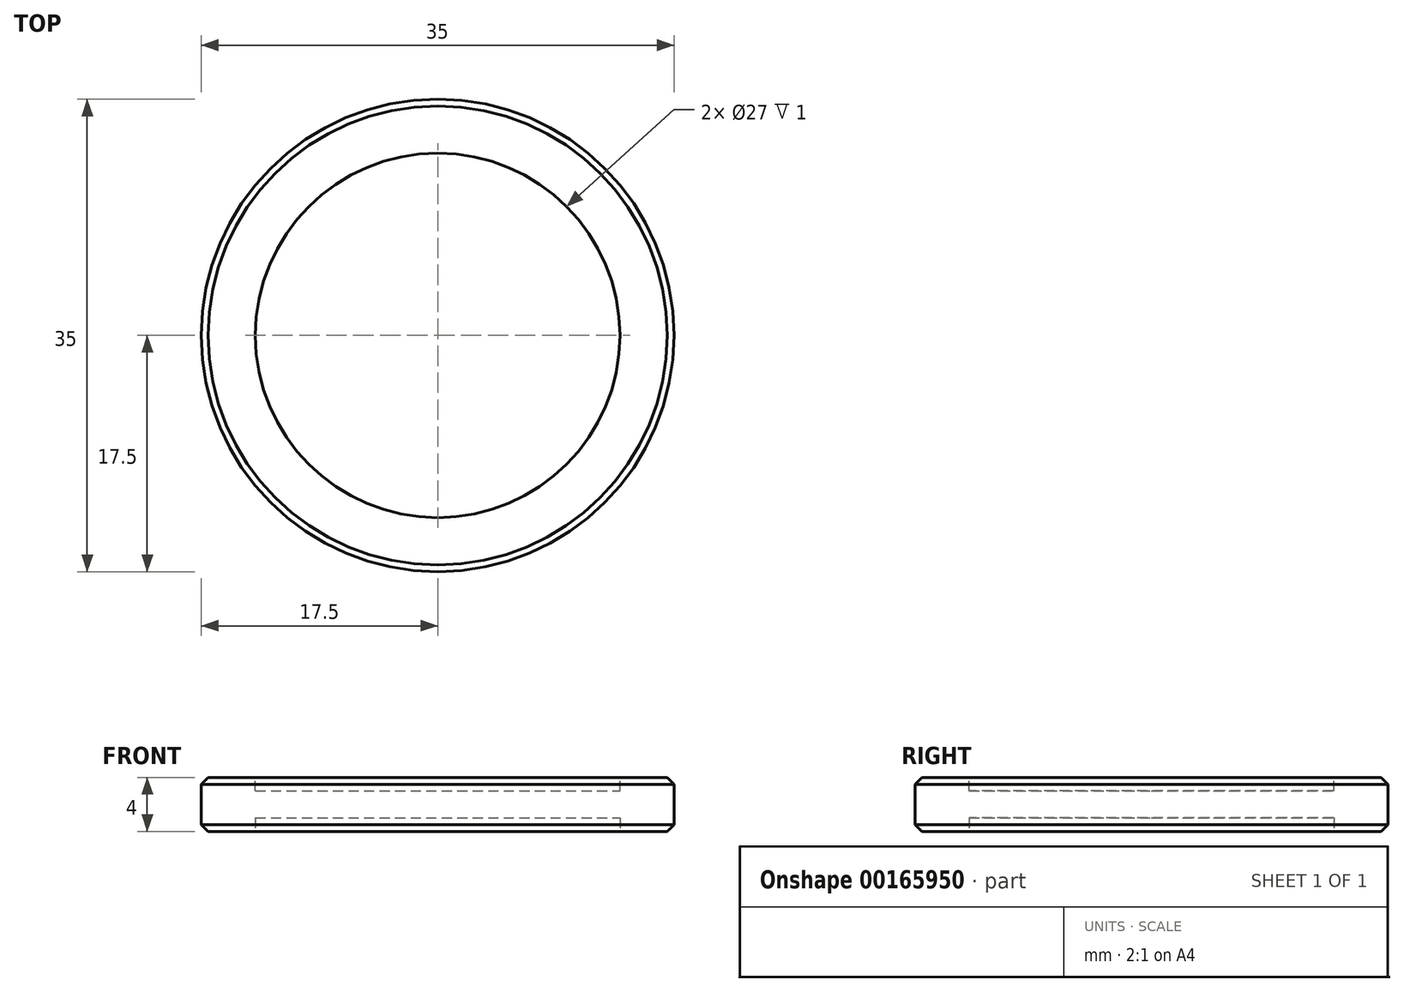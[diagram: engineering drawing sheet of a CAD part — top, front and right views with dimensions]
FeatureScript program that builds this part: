
annotation { "Feature Type Name" : "Feature", "Feature Type Description" : "" }
export const myFeature = defineFeature(function(context is Context, id is Id, definition is map)
    precondition{}
    {
        {
            var Q0;
            Q0=qCreatedBy(makeId("Top.planeOp"),FACE);
            var sketch = newSketch(context, id + "F0", { "sketchPlane" : qUnion([Q0])});
            skCircle(sketch, "E0", {"center": v(0, 0) * mm, "radius": 17.5 * mm});
            skSolve(sketch);
        }
        {
            var Q0;
            Q0 = qSketchRegion(id + "F0", true);
            extrude(context, id + "F1", {"entities" : qUnion([Q0]), "depth" : 2 * mm});
        }
        {
            var Q0;
            Q0=makeQuery(id+"F1.opExtrude","CAP_FACE",FACE,{"disambiguationData":[OSD([sQuery(id+"F0.wireOp",EDGE,"E0")])],"isStart":true});
            var sketch = newSketch(context, id + "F2", { "sketchPlane" : qUnion([Q0])});
            skCircle(sketch, "E1", {"center": v(0, 0) * mm, "radius": 13.5 * mm});
            skSolve(sketch);
        }
        {
            var Q0;
            Q0=makeQuery(id+"F2.imprint","IMPRINT",FACE,{"disambiguationData":[TD([[makeQuery(id+"F2.imprint","IMPRINT",EDGE,{"derivedFrom":sQuery(id+"F2.wireOp",EDGE,"E1")}),1.0]])]});
            var Q1;
            Q1=sQuery(id+"F2.wireOp",EDGE,"E1");
            extrude(context, id + "F3", {"entities" : qUnion([Q0]), "operationType" : NewBodyOperationType.REMOVE, "surfaceEntities" : qUnion([Q1]), "oppositeDirection" : true, "depth" : 1 * mm});
        }
        {
            var Q0;
            Q0=makeQuery(id+"F1.opExtrude","SWEPT_BODY",BODY,{"disambiguationData":[OSD([sQuery(id+"F0.wireOp",EDGE,"E0")])]});
            var Q1;
            Q1=makeQuery(id+"F1.opExtrude","CAP_FACE",FACE,{"disambiguationData":[OSD([sQuery(id+"F0.wireOp",EDGE,"E0")])],"isStart":false});
            mirror(context, id + "F4", {"operationType" : NewBodyOperationType.ADD, "entities" : qUnion([Q0]), "mirrorPlane" : qUnion([Q1])});
        }
        {
            var Q0;
            {var subQ0=makeQuery(id+"F1.opExtrude","SWEPT_FACE",FACE,{"disambiguationData":[OSD([sQuery(id+"F0.wireOp",EDGE,"E0")])]});Q0=makeQuery(id+"F4.boolean.opBoolean","MERGE",FACE,{"derivedFrom":[subQ0,makeQuery(id+"F4.opPattern","COPY",FACE,{"derivedFrom":subQ0,"instanceName":"1"})]});}
            chamfer(context, id + "F5", {"entities" : qUnion([Q0]), "width" : 0.5 * mm, "tangentPropagation" : true});
        }
    });
